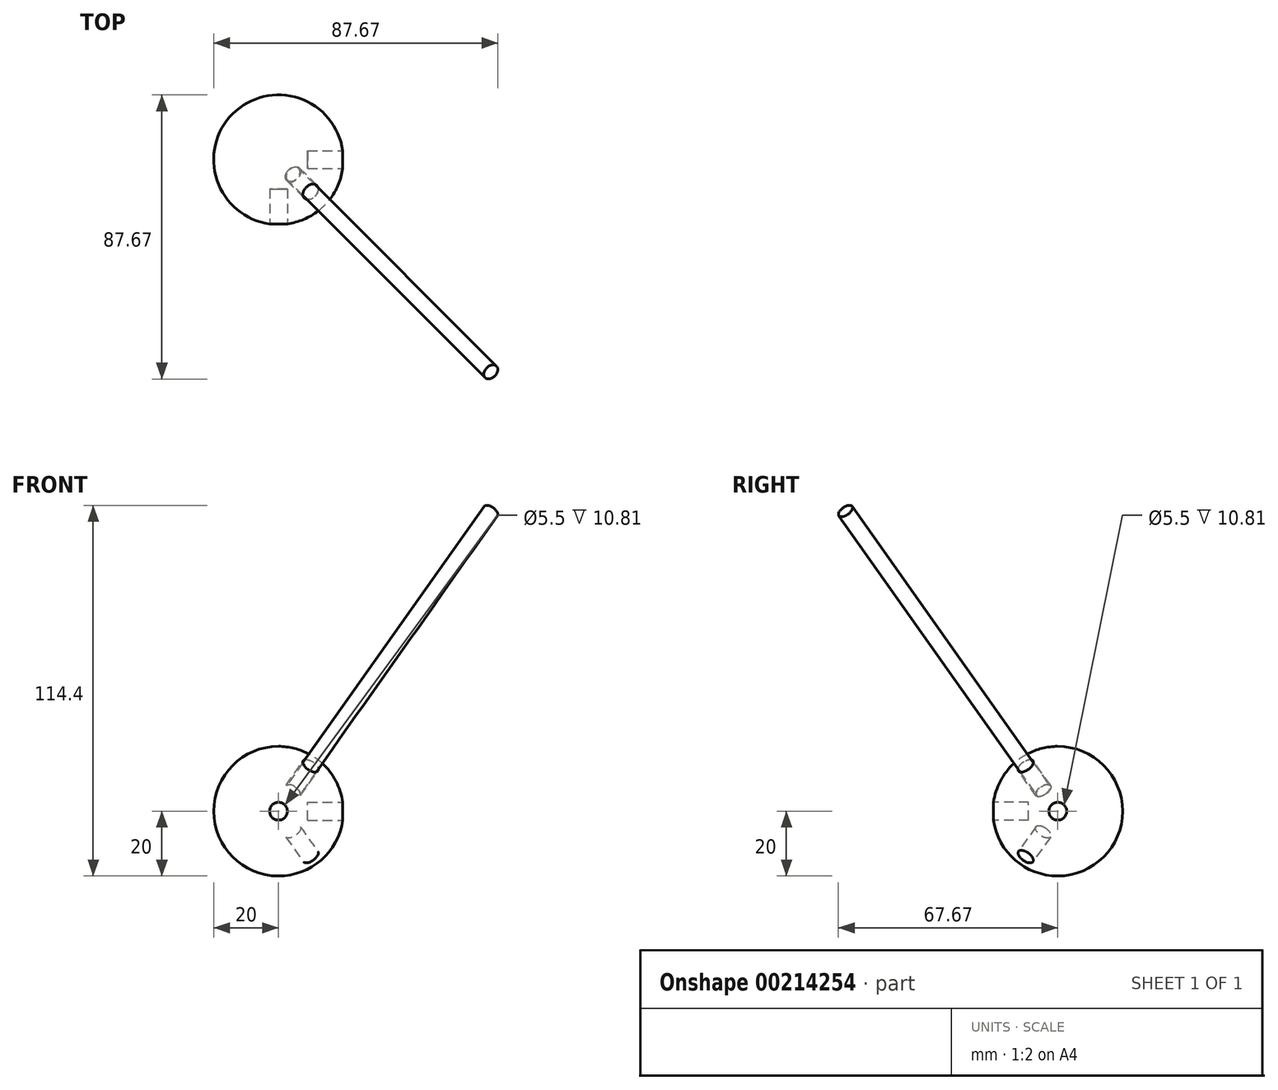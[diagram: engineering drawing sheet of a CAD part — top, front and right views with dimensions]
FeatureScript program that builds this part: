
annotation { "Feature Type Name" : "Feature", "Feature Type Description" : "" }
export const myFeature = defineFeature(function(context is Context, id is Id, definition is map)
    precondition{}
    {
        {
            assignVariable(context, id + "F0", {"name" : "D", "anyValue" : 40});
        }
        {
            assignVariable(context, id + "F1", {"name" : "d", "anyValue" : 5.5});
        }
        {
            assignVariable(context, id + "F2", {"name" : "L", "anyValue" : 122});
        }
        {
            var Q0;
            Q0=qCreatedBy(makeId("Front.planeOp"),FACE);
            var sketch = newSketch(context, id + "F3", { "sketchPlane" : qUnion([Q0])});
            skArc(sketch, "E0", {"start": v(0, -20) * mm, "mid": v(-20, 0) * mm, "end": v(0, 20) * mm});
            skLineSegment(sketch, "E1", {"start": v(0, 20) * mm, "end": v(0, -20) * mm});
            skSolve(sketch);
        }
        {
            var Q0;
            Q0=qSketchRegion(id+"F3",true);
            var Q1;
            Q1=sQuery(id+"F3.wireOp",EDGE,"E1");
            revolve(context, id + "F4", {"entities" : qUnion([Q0]), "axis" : qUnion([Q1]), "revolveType" : RevolveType.FULL});
        }
        {
            var Q0;
            Q0=qCreatedBy(makeId("Front.planeOp"),FACE);
            cPlane(context, id + "F5", {"entities" : qUnion([Q0]), "cplaneType" : CPlaneType.OFFSET, "offset" : (getVariable(context, 'D') / 2) * mm, "width" : 150 * mm, "height" : 150 * mm});
        }
        {
            var Q0;
            Q0=qCreatedBy(id+"F5.planeOp",FACE);
            var sketch = newSketch(context, id + "F6", { "sketchPlane" : qUnion([Q0])});
            skCircle(sketch, "E2", {"center": v(0, 0) * mm, "radius": 2.75 * mm});
            skSolve(sketch);
        }
        {
            var Q0;
            Q0=qSketchRegion(id+"F6",true);
            extrude(context, id + "F7", {"entities" : qUnion([Q0]), "operationType" : NewBodyOperationType.REMOVE, "oppositeDirection" : true, "depth" : (getVariable(context, 'd') * 2) * mm});
        }
        {
            var Q0;
            Q0=qCreatedBy(makeId("Right.planeOp"),FACE);
            cPlane(context, id + "F8", {"entities" : qUnion([Q0]), "cplaneType" : CPlaneType.OFFSET, "offset" : (getVariable(context, 'D') / 2) * mm, "width" : 150 * mm, "height" : 150 * mm});
        }
        {
            var Q0;
            Q0=qCreatedBy(id+"F8.planeOp",FACE);
            var sketch = newSketch(context, id + "F9", { "sketchPlane" : qUnion([Q0])});
            skCircle(sketch, "E3", {"center": v(0, 0) * mm, "radius": 2.75 * mm});
            skSolve(sketch);
        }
        {
            var Q0;
            Q0 = qSketchRegion(id + "F9", true);
            extrude(context, id + "F10", {"entities" : qUnion([Q0]), "operationType" : NewBodyOperationType.REMOVE, "oppositeDirection" : true, "depth" : (getVariable(context, 'd') * 2) * mm});
        }
        {
            var Q0;
            Q0=qCreatedBy(id+"F8.planeOp",FACE);
            var Q1;
            Q1=qCreatedBy(id+"F5.planeOp",FACE);
            cPlane(context, id + "F11", {"entities" : qUnion([Q0, Q1]), "cplaneType" : CPlaneType.MID_PLANE, "offset" : 25 * mm, "width" : 150 * mm, "height" : 150 * mm});
        }
        {
            var Q0;
            Q0=qCreatedBy(id+"F11.planeOp",FACE);
            var sketch = newSketch(context, id + "F12", { "sketchPlane" : qUnion([Q0])});
            skCircle(sketch, "E4.cCircle", {"center": v(0, 0) * mm, "radius": 10 * mm, "construction": true});
            skLineSegment(sketch, "E4.0", {"start": v(-5.18, -19.32) * mm, "end": v(-14.14, 14.14) * mm, "construction": true});
            skLineSegment(sketch, "E4.1", {"start": v(-14.14, 14.14) * mm, "end": v(19.32, 5.18) * mm, "construction": true});
            skLineSegment(sketch, "E4.2", {"start": v(19.32, 5.18) * mm, "end": v(-5.18, -19.32) * mm, "construction": true});
            skPoint(sketch, "E4.0.midPoint", {"position": v(-9.66, -2.59) * mm});
            skLineSegment(sketch, "E5", {"start": v(-14.14, 14.14) * mm, "end": v(0, 0) * mm, "construction": true});
            skLineSegment(sketch, "E6", {"start": v(0, 0) * mm, "end": v(-22.28, 0) * mm, "construction": true});
            skLineSegment(sketch, "E7.0", {"start": v(19.32, -5.18) * mm, "end": v(-14.14, -14.14) * mm, "construction": true});
            skLineSegment(sketch, "E7.1", {"start": v(-14.14, -14.14) * mm, "end": v(-5.18, 19.32) * mm, "construction": true});
            skLineSegment(sketch, "E7.2", {"start": v(-5.18, 19.32) * mm, "end": v(19.32, -5.18) * mm, "construction": true});
            skPoint(sketch, "E7.0.midPoint", {"position": v(2.59, -9.66) * mm});
            skLineSegment(sketch, "E8", {"start": v(-14.14, -14.14) * mm, "end": v(0, 0) * mm, "construction": true});
            skSolve(sketch);
        }
        {
            var Q0;
            Q0=sQuery(id+"F12.wireOp",VERTEX,"E4.1.start");
            var Q1;
            Q1=sQuery(id+"F12.wireOp",EDGE,"E5");
            cPlane(context, id + "F13", {"entities" : qUnion([Q0, Q1]), "cplaneType" : CPlaneType.LINE_POINT, "offset" : 25 * mm, "width" : 150 * mm, "height" : 150 * mm});
        }
        {
            var Q0;
            Q0=qCreatedBy(id+"F13.planeOp",FACE);
            var sketch = newSketch(context, id + "F14", { "sketchPlane" : qUnion([Q0])});
            skCircle(sketch, "E9", {"center": v(0, 0) * mm, "radius": 2.75 * mm});
            skSolve(sketch);
        }
        {
            var Q0;
            Q0 = qSketchRegion(id + "F14", true);
            extrude(context, id + "F15", {"entities" : qUnion([Q0]), "operationType" : NewBodyOperationType.REMOVE, "depth" : (getVariable(context, 'd') * 2) * mm});
        }
        {
            var Q0;
            Q0=sQuery(id+"F12.wireOp",VERTEX,"E7.1.start");
            var Q1;
            Q1=sQuery(id+"F12.wireOp",EDGE,"E8");
            cPlane(context, id + "F16", {"entities" : qUnion([Q0, Q1]), "cplaneType" : CPlaneType.LINE_POINT, "offset" : 25 * mm, "width" : 150 * mm, "height" : 150 * mm});
        }
        {
            var Q0;
            Q0=qCreatedBy(id+"F16.planeOp",FACE);
            var sketch = newSketch(context, id + "F17", { "sketchPlane" : qUnion([Q0])});
            skCircle(sketch, "E10", {"center": v(0, 0) * mm, "radius": 2.75 * mm});
            skSolve(sketch);
        }
        {
            var Q0;
            Q0 = qSketchRegion(id + "F17", true);
            extrude(context, id + "F18", {"entities" : qUnion([Q0]), "operationType" : NewBodyOperationType.REMOVE, "depth" : (getVariable(context, 'd') * 2) * mm});
        }
        {
            var Q0;
            Q0=makeQuery(id+"F15.boolean.opBoolean","COPY",FACE,{"derivedFrom":makeQuery(id+"F15.opExtrude","CAP_FACE",FACE,{"disambiguationData":[OSD([sQuery(id+"F14.wireOp",EDGE,"E9")])],"isStart":false})});
            var sketch = newSketch(context, id + "F19", { "sketchPlane" : qUnion([Q0])});
            skCircle(sketch, "E11", {"center": v(0, 0) * mm, "radius": 2.5 * mm});
            skSolve(sketch);
        }
        {
            var Q0;
            Q0 = qSketchRegion(id + "F19", true);
            extrude(context, id + "F20", {"entities" : qUnion([Q0]), "depth" : (getVariable(context, 'L')) * mm});
        }
    });
